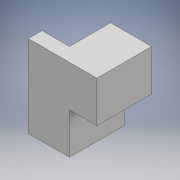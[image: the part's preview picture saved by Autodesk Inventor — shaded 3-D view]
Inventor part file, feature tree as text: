
AUTODESK INVENTOR PART (.ipt)
format: ipt  version: 2018 (Build 220112000, 112)  size: 112,128 bytes
history: native  units: mm
features: extrude x3, sketch x2
ambient origin geometry x8: Origin, YZ Plane, XZ Plane, XY Plane, X Axis, Y Axis, Z Axis, Center Point
bodies: Solid1 (feature_tree)
feature tree (5):
  sketch  "Sketch3"  dims[d12=25.0mm d13=5.0mm]
  extrude  "Extrusion1"  Depth=5.0mm
  extrude  "Extrusion2"  Depth=15.0mm
  extrude  "Extrusion3"  Depth=15.0mm
  sketch  "Sketch4"  dims[d14=10.0mm d15=15.0mm d16=15.0mm d17=15.0mm d18=0.0mm d19=10.0mm d20=15.0mm d21=0.0mm d22=5.0mm d23=0.0mm]
